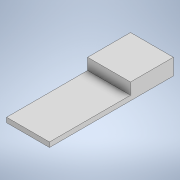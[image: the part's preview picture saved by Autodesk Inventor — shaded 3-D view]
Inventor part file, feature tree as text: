
AUTODESK INVENTOR PART (.ipt)
format: ipt  version: 2022 (Build 260153000, 153)  size: 103,424 bytes
history: native  units: in
note: dims shown in document units (in); Inventor stores cm internally (conversion verified against a paired STEP export)
features: extrude x2, sketch x2
ambient origin geometry x8: Origin, YZ Plane, XZ Plane, XY Plane, X Axis, Y Axis, Z Axis, Center Point
bodies: Solid1 (feature_tree)
feature tree (4):
  extrude  "Extrusion1"  Depth=5.1181in
  extrude  "Extrusion2"  Depth=1.7717in
  sketch  "Sketch1"  dims[d0=1.7717in d1=5.1181in]
  sketch  "Sketch2"  dims[d2=0.1969in d3=0.0in d4=1.7717in d5=0.4724in d6=0.0in]
